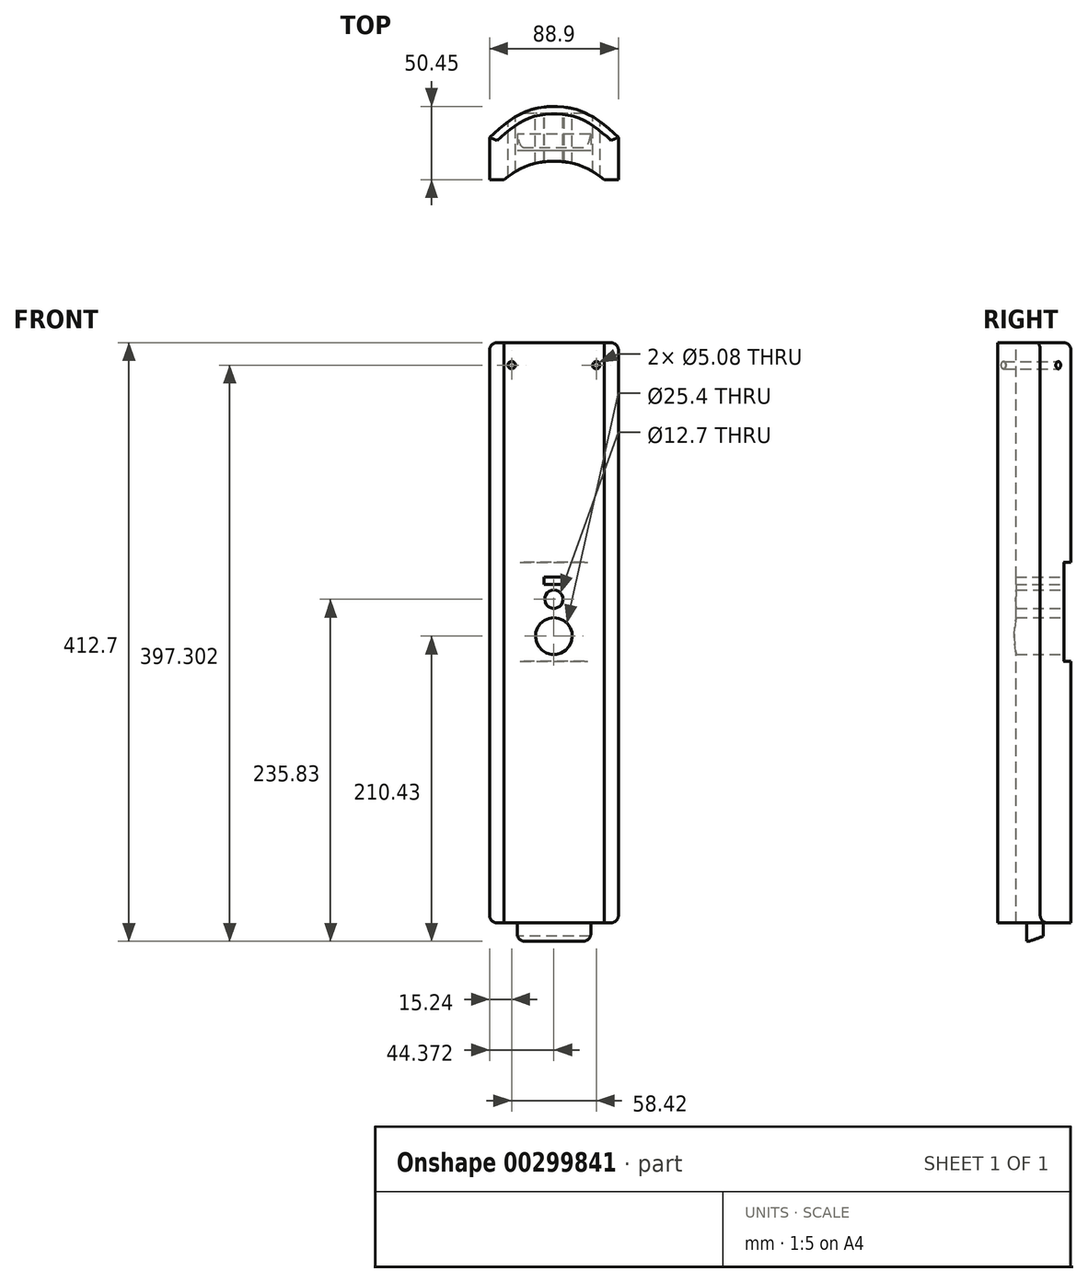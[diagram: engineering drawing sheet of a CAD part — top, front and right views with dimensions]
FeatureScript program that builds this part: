
annotation { "Feature Type Name" : "Feature", "Feature Type Description" : "" }
export const myFeature = defineFeature(function(context is Context, id is Id, definition is map)
    precondition{}
    {
        {
            var Q0;
            Q0=qCreatedBy(makeId("Front.planeOp"),FACE);
            var sketch = newSketch(context, id + "F0", { "sketchPlane" : qUnion([Q0])});
            skLineSegment(sketch, "E0.bottom", {"start": v(0, 0) * mm, "end": v(88.9, 0) * mm});
            skLineSegment(sketch, "E0.top", {"start": v(0, 400) * mm, "end": v(88.9, 400) * mm});
            skLineSegment(sketch, "E0.left", {"start": v(0, 0) * mm, "end": v(0, 400) * mm});
            skLineSegment(sketch, "E0.right", {"start": v(88.9, 0) * mm, "end": v(88.9, 400) * mm});
            skSolve(sketch);
        }
        {
            var Q0;
            Q0 = qSketchRegion(id + "F0", true);
            extrude(context, id + "F1", {"entities" : qUnion([Q0]), "depth" : 58.42 * mm});
        }
        {
            var Q0;
            Q0=qCreatedBy(makeId("Top.planeOp"),FACE);
            var sketch = newSketch(context, id + "F2", { "sketchPlane" : qUnion([Q0])});
            skLineSegment(sketch, "E1", {"start": v(22.22, 35.23) * mm, "end": v(22.23, -117.17) * mm, "construction": true});
            skLineSegment(sketch, "E2", {"start": v(44.45, 35.23) * mm, "end": v(44.45, -117.17) * mm, "construction": true});
            skLineSegment(sketch, "E3", {"start": v(66.67, 35.23) * mm, "end": v(66.67, -117.17) * mm, "construction": true});
            skFitSpline(sketch, "E4", {"points": [v(0, -66.96) * mm, v(22.23, -50.44) * mm, v(44.45, -45.73) * mm, v(66.67, -50.44) * mm, v(88.9, -66.96) * mm], "startDerivative": vector(82.2, 73.14) * mm, "endDerivative": vector(80.14, -75.3) * mm});
            skLineSegment(sketch, "E5", {"start": v(88.9, -66.96) * mm, "end": v(0, -66.96) * mm});
            skFitSpline(sketch, "E6", {"points": [v(0, -29.21) * mm, v(22.22, -12.7) * mm, v(44.45, -7.97) * mm, v(66.67, -12.7) * mm, v(88.9, -29.21) * mm], "startDerivative": vector(82.2, 73.14) * mm, "endDerivative": vector(80.14, -75.3) * mm});
            skLineSegment(sketch, "E7", {"start": v(113.45, -29.2) * mm, "end": v(-92.88, -29.21) * mm, "construction": true});
            skLineSegment(sketch, "E8", {"start": v(88.9, -29.21) * mm, "end": v(88.9, 0) * mm});
            skLineSegment(sketch, "E9", {"start": v(88.9, 0) * mm, "end": v(0, 0) * mm});
            skLineSegment(sketch, "E10", {"start": v(0, 0) * mm, "end": v(0, -29.21) * mm});
            skSolve(sketch);
        }
        {
            var Q0;
            Q0=makeQuery(id+"F2.imprint","IMPRINT",FACE,{"disambiguationData":[TD([[makeQuery(id+"F2.imprint","IMPRINT",EDGE,{"derivedFrom":sQuery(id+"F2.wireOp",EDGE,"E4")}),-1.0]])]});
            extrude(context, id + "F3", {"entities" : qUnion([Q0]), "operationType" : NewBodyOperationType.REMOVE, "endBound" : BoundingType.THROUGH_ALL, "depth" : 25.4 * mm});
        }
        {
            var Q0;
            Q0=makeQuery(id+"F2.imprint","IMPRINT",FACE,{"disambiguationData":[TD([[makeQuery(id+"F2.imprint","IMPRINT",EDGE,{"derivedFrom":sQuery(id+"F2.wireOp",EDGE,"E6")}),1.0]])]});
            extrude(context, id + "F4", {"entities" : qUnion([Q0]), "operationType" : NewBodyOperationType.REMOVE, "endBound" : BoundingType.THROUGH_ALL, "depth" : 25.4 * mm});
        }
        {
            var Q0;
            Q0=qCreatedBy(makeId("Top.planeOp"),FACE);
            var sketch = newSketch(context, id + "F5", { "sketchPlane" : qUnion([Q0])});
            skLineSegment(sketch, "E11.bottom", {"start": v(69.85, -27) * mm, "end": v(19.05, -27) * mm});
            skLineSegment(sketch, "E11.top", {"start": v(69.85, -38.43) * mm, "end": v(19.05, -38.43) * mm});
            skLineSegment(sketch, "E11.left", {"start": v(69.85, -27) * mm, "end": v(69.85, -38.43) * mm});
            skLineSegment(sketch, "E11.right", {"start": v(19.05, -27) * mm, "end": v(19.05, -38.43) * mm});
            skSolve(sketch);
        }
        {
            var Q0;
            Q0=makeQuery(id+"F5.imprint","IMPRINT",FACE,{"disambiguationData":[TD([[makeQuery(id+"F5.imprint","IMPRINT",EDGE,{"derivedFrom":sQuery(id+"F5.wireOp",EDGE,"E11.bottom")}),1.0]])]});
            extrude(context, id + "F6", {"entities" : qUnion([Q0]), "operationType" : NewBodyOperationType.ADD, "oppositeDirection" : true, "depth" : 12.7 * mm});
        }
        {
            var Q0;
            Q0=qCreatedBy(makeId("Right.planeOp"),FACE);
            var sketch = newSketch(context, id + "F7", { "sketchPlane" : qUnion([Q0])});
            skLineSegment(sketch, "E12", {"start": v(-27, -9.25) * mm, "end": v(-36.55, -12.7) * mm});
            skLineSegment(sketch, "E13", {"start": v(-27, -9.25) * mm, "end": v(-27, -12.7) * mm});
            skLineSegment(sketch, "E14", {"start": v(-27, -12.7) * mm, "end": v(-36.55, -12.7) * mm});
            skSolve(sketch);
        }
        {
            var Q0;
            Q0=makeQuery(id+"F7.imprint","IMPRINT",FACE,{"disambiguationData":[TD([[makeQuery(id+"F7.imprint","IMPRINT",EDGE,{"derivedFrom":sQuery(id+"F7.wireOp",EDGE,"E12")}),1.0]])]});
            extrude(context, id + "F8", {"entities" : qUnion([Q0]), "operationType" : NewBodyOperationType.REMOVE, "endBound" : BoundingType.THROUGH_ALL, "depth" : 25.4 * mm});
        }
        {
            var Q0;
            Q0=qCreatedBy(makeId("Front.planeOp"),FACE);
            var sketch = newSketch(context, id + "F9", { "sketchPlane" : qUnion([Q0])});
            skLineSegment(sketch, "E15.bottom", {"start": v(68.58, 248.53) * mm, "end": v(20.32, 248.53) * mm});
            skLineSegment(sketch, "E15.top", {"start": v(68.58, 180.27) * mm, "end": v(20.32, 180.27) * mm});
            skLineSegment(sketch, "E15.left", {"start": v(68.58, 248.53) * mm, "end": v(68.58, 180.27) * mm});
            skLineSegment(sketch, "E15.right", {"start": v(20.32, 248.53) * mm, "end": v(20.32, 180.27) * mm});
            skSolve(sketch);
        }
        {
            var Q0;
            Q0=makeQuery(id+"F9.imprint","IMPRINT",FACE,{"disambiguationData":[TD([[makeQuery(id+"F9.imprint","IMPRINT",EDGE,{"derivedFrom":sQuery(id+"F9.wireOp",EDGE,"E15.bottom")}),1.0]])]});
            extrude(context, id + "F10", {"entities" : qUnion([Q0]), "operationType" : NewBodyOperationType.REMOVE, "depth" : 12.7 * mm});
        }
        {
            var Q0;
            Q0=qCreatedBy(makeId("Front.planeOp"),FACE);
            var sketch = newSketch(context, id + "F11", { "sketchPlane" : qUnion([Q0])});
            skLineSegment(sketch, "E16.bottom", {"start": v(51.43, 238.37) * mm, "end": v(37.47, 238.37) * mm});
            skLineSegment(sketch, "E16.top", {"start": v(51.43, 233.29) * mm, "end": v(37.47, 233.29) * mm});
            skLineSegment(sketch, "E16.left", {"start": v(51.43, 238.37) * mm, "end": v(51.43, 233.29) * mm});
            skLineSegment(sketch, "E16.right", {"start": v(37.47, 238.37) * mm, "end": v(37.47, 233.29) * mm});
            skCircle(sketch, "E17", {"center": v(44.37, 223.13) * mm, "radius": 6.35 * mm});
            skCircle(sketch, "E18", {"center": v(44.37, 197.73) * mm, "radius": 12.7 * mm});
            skLineSegment(sketch, "E19", {"start": v(44.37, 261.29) * mm, "end": v(44.37, 191.42) * mm, "construction": true});
            skSolve(sketch);
        }
        {
            var Q0;
            Q0=makeQuery(id+"F11.imprint","IMPRINT",FACE,{"disambiguationData":[TD([[makeQuery(id+"F11.imprint","IMPRINT",EDGE,{"derivedFrom":sQuery(id+"F11.wireOp",EDGE,"E16.bottom")}),1.0]])]});
            var Q1;
            Q1=makeQuery(id+"F11.imprint","IMPRINT",FACE,{"disambiguationData":[TD([[makeQuery(id+"F11.imprint","IMPRINT",EDGE,{"derivedFrom":sQuery(id+"F11.wireOp",EDGE,"E17")}),1.0]])]});
            var Q2;
            Q2=makeQuery(id+"F11.imprint","IMPRINT",FACE,{"disambiguationData":[TD([[makeQuery(id+"F11.imprint","IMPRINT",EDGE,{"derivedFrom":sQuery(id+"F11.wireOp",EDGE,"E18")}),1.0]])]});
            extrude(context, id + "F12", {"entities" : qUnion([Q0, Q1, Q2]), "operationType" : NewBodyOperationType.REMOVE, "endBound" : BoundingType.THROUGH_ALL, "depth" : 25.4 * mm});
        }
        {
            var Q0;
            Q0=qCreatedBy(makeId("Front.planeOp"),FACE);
            var sketch = newSketch(context, id + "F13", { "sketchPlane" : qUnion([Q0])});
            skCircle(sketch, "E20", {"center": v(73.66, 384.6) * mm, "radius": 2.54 * mm});
            skCircle(sketch, "E21", {"center": v(15.24, 384.6) * mm, "radius": 2.54 * mm});
            skLineSegment(sketch, "E22", {"start": v(93.45, 399.84) * mm, "end": v(-17.43, 399.84) * mm});
            skSolve(sketch);
        }
        {
            var Q0;
            Q0=makeQuery(id+"F13.imprint","IMPRINT",FACE,{"disambiguationData":[TD([[makeQuery(id+"F13.imprint","IMPRINT",EDGE,{"derivedFrom":sQuery(id+"F13.wireOp",EDGE,"E20")}),1.0]])]});
            var Q1;
            Q1=makeQuery(id+"F13.imprint","IMPRINT",FACE,{"disambiguationData":[TD([[makeQuery(id+"F13.imprint","IMPRINT",EDGE,{"derivedFrom":sQuery(id+"F13.wireOp",EDGE,"E21")}),1.0]])]});
            extrude(context, id + "F14", {"entities" : qUnion([Q0, Q1]), "operationType" : NewBodyOperationType.REMOVE, "endBound" : BoundingType.THROUGH_ALL, "depth" : 25.4 * mm});
        }
        {
            var Q0;
            Q0=makeQuery(id+"F4.boolean.opBoolean","COPY",EDGE,{"derivedFrom":makeQuery(id+"F4.opExtrude","SWEPT_EDGE",EDGE,{"disambiguationData":[OSD([sQuery(id+"F2.wireOp",EDGE,"E6"),sQuery(id+"F2.wireOp",EDGE,"E8")])]})});
            var Q1;
            Q1=makeQuery(id+"F4.boolean.opBoolean","COPY",EDGE,{"derivedFrom":makeQuery(id+"F4.opExtrude","SWEPT_EDGE",EDGE,{"disambiguationData":[OSD([sQuery(id+"F2.wireOp",EDGE,"E6"),sQuery(id+"F2.wireOp",EDGE,"E10")])]})});
            var Q2;
            Q2=makeQuery(id+"F4.boolean.opBoolean","COPY",EDGE,{"derivedFrom":makeQuery(id+"F4.opExtrude","CAP_EDGE",EDGE,{"disambiguationData":[OSD([sQuery(id+"F2.wireOp",EDGE,"E6")])],"isStart":true})});
            var Q3;
            Q3=makeQuery(id+"F10.boolean.opBoolean","INTERSECT",EDGE,{"disambiguationData":[OD(1.0)],"derivedFrom":[makeQuery(id+"F4.boolean.opBoolean","COPY",FACE,{"derivedFrom":makeQuery(id+"F4.opExtrude","SWEPT_FACE",FACE,{"disambiguationData":[OSD([sQuery(id+"F2.wireOp",EDGE,"E6")])]})}),makeQuery(id+"F10.opExtrude","CAP_FACE",FACE,{"disambiguationData":[OSD([sQuery(id+"F9.wireOp",EDGE,"E15.bottom"),sQuery(id+"F9.wireOp",EDGE,"E15.top"),sQuery(id+"F9.wireOp",EDGE,"E15.left"),sQuery(id+"F9.wireOp",EDGE,"E15.right")])],"isStart":false})]});
            var Q4;
            Q4=makeQuery(id+"F10.boolean.opBoolean","INTERSECT",EDGE,{"disambiguationData":[OD(0.0)],"derivedFrom":[makeQuery(id+"F4.boolean.opBoolean","COPY",FACE,{"derivedFrom":makeQuery(id+"F4.opExtrude","SWEPT_FACE",FACE,{"disambiguationData":[OSD([sQuery(id+"F2.wireOp",EDGE,"E6")])]})}),makeQuery(id+"F10.opExtrude","CAP_FACE",FACE,{"disambiguationData":[OSD([sQuery(id+"F9.wireOp",EDGE,"E15.bottom"),sQuery(id+"F9.wireOp",EDGE,"E15.top"),sQuery(id+"F9.wireOp",EDGE,"E15.left"),sQuery(id+"F9.wireOp",EDGE,"E15.right")])],"isStart":false})]});
            var Q5;
            Q5=makeQuery(id+"F4.boolean.opBoolean","INTERSECT",EDGE,{"derivedFrom":[makeQuery(id+"F1.opExtrude","SWEPT_FACE",FACE,{"disambiguationData":[OSD([sQuery(id+"F0.wireOp",EDGE,"E0.top")])]}),makeQuery(id+"F4.opExtrude","SWEPT_FACE",FACE,{"disambiguationData":[OSD([sQuery(id+"F2.wireOp",EDGE,"E6")])]})]});
            var Q6;
            Q6=makeQuery(id+"F1.opExtrude","SWEPT_EDGE",EDGE,{"disambiguationData":[OSD([sQuery(id+"F0.wireOp",EDGE,"E0.top"),sQuery(id+"F0.wireOp",EDGE,"E0.right")])]});
            var Q7;
            Q7=makeQuery(id+"F1.opExtrude","SWEPT_EDGE",EDGE,{"disambiguationData":[OSD([sQuery(id+"F0.wireOp",EDGE,"E0.top"),sQuery(id+"F0.wireOp",EDGE,"E0.left")])]});
            var Q8;
            Q8=makeQuery(id+"F1.opExtrude","SWEPT_EDGE",EDGE,{"disambiguationData":[OSD([sQuery(id+"F0.wireOp",EDGE,"E0.bottom"),sQuery(id+"F0.wireOp",EDGE,"E0.right")])]});
            var Q9;
            Q9=makeQuery(id+"F1.opExtrude","SWEPT_EDGE",EDGE,{"disambiguationData":[OSD([sQuery(id+"F0.wireOp",EDGE,"E0.bottom"),sQuery(id+"F0.wireOp",EDGE,"E0.left")])]});
            var Q10;
            Q10=makeQuery(id+"F6.opExtrude","CAP_EDGE",EDGE,{"disambiguationData":[OSD([sQuery(id+"F5.wireOp",EDGE,"E11.left")])],"isStart":false});
            var Q11;
            Q11=makeQuery(id+"F6.opExtrude","CAP_EDGE",EDGE,{"disambiguationData":[OSD([sQuery(id+"F5.wireOp",EDGE,"E11.right")])],"isStart":false});
            fillet(context, id + "F15", {"entities" : qUnion([Q0, Q1, Q2, Q3, Q4, Q5, Q6, Q7, Q8, Q9, Q10, Q11]), "radius" : 5.08 * mm, "tangentPropagation" : true, "allowEdgeOverflow" : false});
        }
    });
